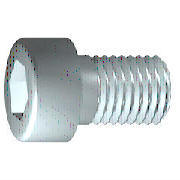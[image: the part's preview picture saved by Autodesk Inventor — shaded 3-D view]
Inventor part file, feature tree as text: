
AUTODESK INVENTOR PART (.ipt)
format: ipt  version: 2022 (Build 260153000, 153)  size: 199,680 bytes
history: native  units: mm (DEFAULTED — no unit token found)
features: sketch x2, other x1, extrude x1, plane x1, fillet x1
ambient origin geometry x7: Origin, YZ Plane, XY Plane, X Axis, Y Axis, Z Axis, Center Point
bodies: Solid1 (feature_tree)
feature tree (6):
  other  "Cuerpo"
  extrude  "Ranura"  Depth=6.0mm
  plane  "Work Plane1"
  fillet  "Fillet2"  Radius=6.0mm
  sketch  "Boceto1"  dims[d1=7.5mm d2=0.61355mm d3=6.0mm]
  sketch  "Boceto2"  dims[d4=3.0mm d5=60.0deg d6=6.0mm d7=6.0mm d8=5.773503mm d9=10.0mm d10=90.0deg d11=10.0mm d12=0.0mm d13=7.5mm d14=0.0mm d15=0.61345mm d16=0.61345mm d17=0.6mm d19=0.0mm d26=10.0mm d27=45.0deg d28=0.0mm d29=0.0mm d30=0.1mm]
